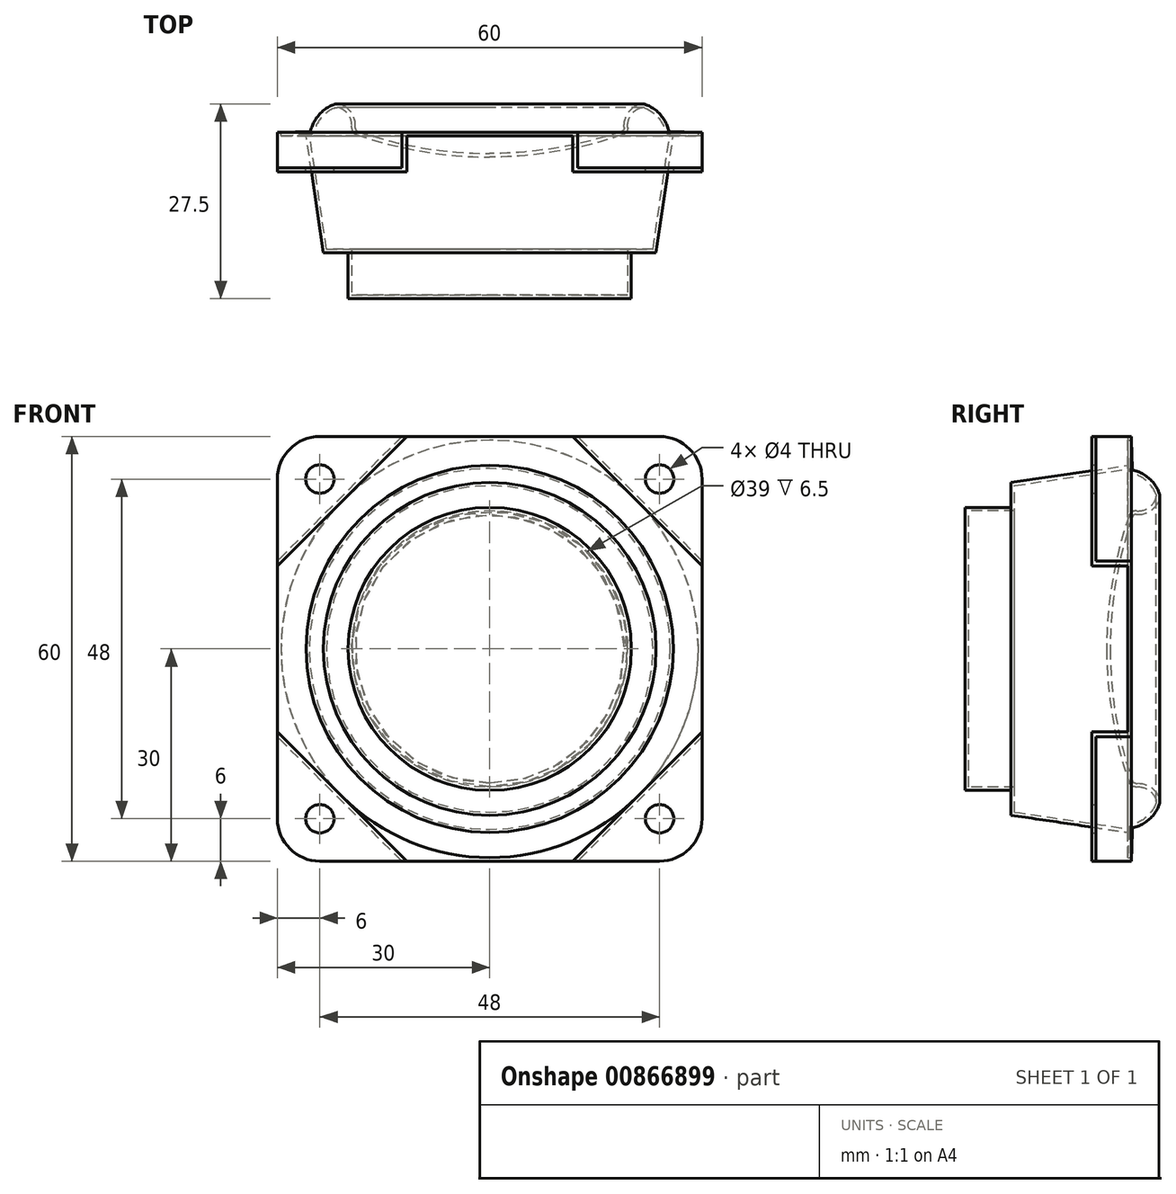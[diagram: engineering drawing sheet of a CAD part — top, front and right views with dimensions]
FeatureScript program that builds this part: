
annotation { "Feature Type Name" : "Feature", "Feature Type Description" : "" }
export const myFeature = defineFeature(function(context is Context, id is Id, definition is map)
    precondition{}
    {
        {
            var Q0;
            Q0=qCreatedBy(makeId("Front.planeOp"),FACE);
            var sketch = newSketch(context, id + "F0", { "sketchPlane" : qUnion([Q0])});
            skLineSegment(sketch, "E0.bottom", {"start": v(24, -30) * mm, "end": v(-24, -30) * mm});
            skLineSegment(sketch, "E0.top", {"start": v(24, 30) * mm, "end": v(-24, 30) * mm});
            skLineSegment(sketch, "E0.left", {"start": v(30, -24) * mm, "end": v(30, 24) * mm});
            skLineSegment(sketch, "E0.right", {"start": v(-30, -24) * mm, "end": v(-30, 24) * mm});
            skPoint(sketch, "E0.middle", {"position": v(0, 0) * mm});
            skPoint(sketch, "E1.visualSharp", {"position": v(-30, 30) * mm});
            skArc(sketch, "E1.filletArc", {"start": v(-24, 30) * mm, "mid": v(-28.24, 28.24) * mm, "end": v(-30, 24) * mm});
            skPoint(sketch, "E2.visualSharp", {"position": v(-30, -30) * mm});
            skArc(sketch, "E2.filletArc", {"start": v(-30, -24) * mm, "mid": v(-28.24, -28.24) * mm, "end": v(-24, -30) * mm});
            skPoint(sketch, "E3.visualSharp", {"position": v(30, -30) * mm});
            skArc(sketch, "E3.filletArc", {"start": v(24, -30) * mm, "mid": v(28.24, -28.24) * mm, "end": v(30, -24) * mm});
            skPoint(sketch, "E4.visualSharp", {"position": v(30, 30) * mm});
            skArc(sketch, "E4.filletArc", {"start": v(30, 24) * mm, "mid": v(28.24, 28.24) * mm, "end": v(24, 30) * mm});
            skLineSegment(sketch, "E5", {"start": v(-24, 24) * mm, "end": v(0, 0) * mm, "construction": true});
            skCircle(sketch, "E6", {"center": v(-24, 24) * mm, "radius": 2 * mm});
            skCircle(sketch, "E7", {"center": v(0, 0) * mm, "radius": 25.5 * mm});
            skCircle(sketch, "E8.1.0", {"center": v(-24, -24) * mm, "radius": 2 * mm});
            skCircle(sketch, "E8.2.0", {"center": v(24, -24) * mm, "radius": 2 * mm});
            skCircle(sketch, "E8.3.0", {"center": v(24, 24) * mm, "radius": 2 * mm});
            skSolve(sketch);
        }
        {
            var Q0;
            Q0 = qSketchRegion(id + "F0", true);
            extrude(context, id + "F1", {"entities" : qUnion([Q0]), "depth" : 5.6 * mm, "offsetDistance" : 25 * mm});
        }
        {
            var Q0;
            Q0=qCreatedBy(makeId("Front.planeOp"),FACE);
            var sketch = newSketch(context, id + "F2", { "sketchPlane" : qUnion([Q0])});
            skLineSegment(sketch, "E9.bottom", {"start": v(42.43, 0) * mm, "end": v(0, -42.43) * mm});
            skLineSegment(sketch, "E9.top", {"start": v(0, 42.43) * mm, "end": v(-42.43, 0) * mm});
            skLineSegment(sketch, "E9.left", {"start": v(42.43, 0) * mm, "end": v(0, 42.43) * mm});
            skLineSegment(sketch, "E9.right", {"start": v(0, -42.43) * mm, "end": v(-42.43, 0) * mm});
            skPoint(sketch, "E9.middle", {"position": v(0, 0) * mm});
            skLineSegment(sketch, "E10", {"start": v(-42.43, 0) * mm, "end": v(0, 0) * mm, "construction": true});
            skLineSegment(sketch, "E11.0", {"start": v(0, 41.72) * mm, "end": v(-41.72, 0) * mm});
            skLineSegment(sketch, "E11.1", {"start": v(41.72, 0) * mm, "end": v(0, 41.72) * mm});
            skLineSegment(sketch, "E11.2", {"start": v(41.72, 0) * mm, "end": v(0, -41.72) * mm});
            skLineSegment(sketch, "E11.3", {"start": v(0, -41.72) * mm, "end": v(-41.72, 0) * mm});
            skLineSegment(sketch, "E12.bottom", {"start": v(81.57, -52.25) * mm, "end": v(-81.57, -52.25) * mm});
            skLineSegment(sketch, "E12.top", {"start": v(81.57, 52.25) * mm, "end": v(-81.57, 52.25) * mm});
            skLineSegment(sketch, "E12.left", {"start": v(81.57, -52.25) * mm, "end": v(81.57, 52.25) * mm});
            skLineSegment(sketch, "E12.right", {"start": v(-81.57, -52.25) * mm, "end": v(-81.57, 52.25) * mm});
            skSolve(sketch);
        }
        {
            var Q0;
            Q0=makeQuery(id+"F2.imprint","IMPRINT",FACE,{"disambiguationData":[TD([[makeQuery(id+"F2.imprint","IMPRINT",EDGE,{"derivedFrom":sQuery(id+"F2.wireOp",EDGE,"E9.bottom")}),1.0]])]});
            extrude(context, id + "F3", {"entities" : qUnion([Q0]), "operationType" : NewBodyOperationType.REMOVE, "depth" : 5 * mm, "offsetDistance" : 25 * mm});
        }
        {
            var Q0;
            Q0=makeQuery(id+"F2.imprint","IMPRINT",FACE,{"disambiguationData":[TD([[makeQuery(id+"F2.imprint","IMPRINT",EDGE,{"derivedFrom":sQuery(id+"F2.wireOp",EDGE,"E11.0")}),1.0]])]});
            var Q1;
            Q1=makeQuery(id+"F1.opExtrude","CAP_FACE",FACE,{"disambiguationData":[OSD([sQuery(id+"F0.wireOp",EDGE,"E0.bottom"),sQuery(id+"F0.wireOp",EDGE,"E0.top"),sQuery(id+"F0.wireOp",EDGE,"E0.left"),sQuery(id+"F0.wireOp",EDGE,"E0.right"),sQuery(id+"F0.wireOp",EDGE,"E1.filletArc"),sQuery(id+"F0.wireOp",EDGE,"E2.filletArc"),sQuery(id+"F0.wireOp",EDGE,"E3.filletArc"),sQuery(id+"F0.wireOp",EDGE,"E4.filletArc"),sQuery(id+"F0.wireOp",EDGE,"E6"),sQuery(id+"F0.wireOp",EDGE,"E7"),sQuery(id+"F0.wireOp",EDGE,"E8.1.0"),sQuery(id+"F0.wireOp",EDGE,"E8.2.0"),sQuery(id+"F0.wireOp",EDGE,"E8.3.0")])],"isStart":false});
            extrude(context, id + "F4", {"entities" : qUnion([Q0]), "operationType" : NewBodyOperationType.REMOVE, "endBound" : BoundingType.UP_TO_SURFACE, "depth" : 25 * mm, "endBoundEntityFace" : qUnion([Q1]), "offsetDistance" : 25 * mm, "hasSecondDirection" : true, "secondDirectionOppositeDirection" : false, "secondDirectionDepth" : .5 * mm});
        }
        {
            var Q0;
            Q0=qCreatedBy(makeId("Right.planeOp"),FACE);
            var sketch = newSketch(context, id + "F5", { "sketchPlane" : qUnion([Q0])});
            skLineSegment(sketch, "E13", {"start": v(0, 26) * mm, "end": v(-17, 23.5) * mm});
            skLineSegment(sketch, "E14", {"start": v(-17, 23.5) * mm, "end": v(-17, 20) * mm});
            skLineSegment(sketch, "E15", {"start": v(-17, 20) * mm, "end": v(-23.5, 20) * mm});
            skLineSegment(sketch, "E16", {"start": v(-23.5, 20) * mm, "end": v(-23.5, 0) * mm});
            skLineSegment(sketch, "E17.0", {"start": v(-23, 19.5) * mm, "end": v(-23, 0) * mm});
            skLineSegment(sketch, "E17.1", {"start": v(-16.5, 19.5) * mm, "end": v(-23, 19.5) * mm});
            skLineSegment(sketch, "E17.2", {"start": v(-16.5, 23.07) * mm, "end": v(-16.5, 19.5) * mm});
            skLineSegment(sketch, "E17.3", {"start": v(0, 25.5) * mm, "end": v(-16.5, 23.07) * mm});
            skLineSegment(sketch, "E18", {"start": v(-23.5, 0) * mm, "end": v(-23, 0) * mm});
            skLineSegment(sketch, "E19", {"start": v(0, 26) * mm, "end": v(0, 25.5) * mm});
            skSolve(sketch);
        }
        {
            var Q0;
            Q0=makeQuery(id+"F5.imprint","IMPRINT",FACE,{"disambiguationData":[TD([[makeQuery(id+"F5.imprint","IMPRINT",EDGE,{"derivedFrom":sQuery(id+"F5.wireOp",EDGE,"E13")}),1.0]])]});
            var Q1;
            Q1=sQuery(id+"F5.wireOp",EDGE,"E18");
            revolve(context, id + "F6", {"operationType" : NewBodyOperationType.ADD, "surfaceOperationType" : NewSurfaceOperationType.NEW, "entities" : qUnion([Q0]), "axis" : qUnion([Q1]), "revolveType" : RevolveType.FULL});
        }
        {
            var Q0;
            Q0=qCreatedBy(makeId("Top.planeOp"),FACE);
            var sketch = newSketch(context, id + "F7", { "sketchPlane" : qUnion([Q0])});
            skLineSegment(sketch, "E20", {"start": v(29.5, 0) * mm, "end": v(25.5, 0.14) * mm});
            skArc(sketch, "E21", {"start": v(25.27, 0.33) * mm, "mid": v(24.1, 2.49) * mm, "end": v(22.1, 3.9) * mm});
            skArc(sketch, "E22", {"start": v(22.1, 3.9) * mm, "mid": v(21.54, 4) * mm, "end": v(20.99, 3.9) * mm});
            skArc(sketch, "E23", {"start": v(20.99, 3.9) * mm, "mid": v(19.46, 2.6) * mm, "end": v(19, 0.66) * mm});
            skArc(sketch, "E24", {"start": v(19, 0.66) * mm, "mid": v(18.92, 0.34) * mm, "end": v(18.67, 0.14) * mm});
            skLineSegment(sketch, "E25", {"start": v(0, -3) * mm, "end": v(-5.6, -3) * mm, "construction": true});
            skArc(sketch, "E26", {"start": v(0, -3) * mm, "mid": v(9.46, -2.2) * mm, "end": v(18.67, 0.14) * mm});
            skArc(sketch, "E27", {"start": v(25.5, 0.14) * mm, "mid": v(25.35, 0.2) * mm, "end": v(25.27, 0.33) * mm});
            skLineSegment(sketch, "E28", {"start": v(21.54, 4) * mm, "end": v(24.51, 4) * mm, "construction": true});
            skLineSegment(sketch, "E29.0", {"start": v(29.48, -0.5) * mm, "end": v(25.48, -0.36) * mm});
            skArc(sketch, "E29.1", {"start": v(25.48, -0.36) * mm, "mid": v(25.04, -0.2) * mm, "end": v(24.78, 0.2) * mm});
            skArc(sketch, "E29.2", {"start": v(24.78, 0.2) * mm, "mid": v(23.73, 2.15) * mm, "end": v(21.91, 3.43) * mm});
            skArc(sketch, "E29.3", {"start": v(0, -3.5) * mm, "mid": v(9.55, -2.7) * mm, "end": v(18.83, -0.33) * mm});
            skArc(sketch, "E29.4", {"start": v(19.5, 0.7) * mm, "mid": v(19.34, 0.07) * mm, "end": v(18.83, -0.33) * mm});
            skArc(sketch, "E29.5", {"start": v(21.17, 3.43) * mm, "mid": v(19.88, 2.34) * mm, "end": v(19.5, 0.7) * mm});
            skArc(sketch, "E29.6", {"start": v(21.91, 3.43) * mm, "mid": v(21.54, 3.5) * mm, "end": v(21.17, 3.43) * mm});
            skLineSegment(sketch, "E30", {"start": v(29.48, -0.5) * mm, "end": v(29.5, 0) * mm});
            skLineSegment(sketch, "E31", {"start": v(0, -3.5) * mm, "end": v(0, -3) * mm});
            skSolve(sketch);
        }
        {
            var Q0;
            Q0 = qSketchRegion(id + "F7", true);
            var Q1;
            Q1=sQuery(id+"F7.wireOp",EDGE,"E31");
            revolve(context, id + "F8", {"surfaceOperationType" : NewSurfaceOperationType.NEW, "entities" : qUnion([Q0]), "axis" : qUnion([Q1]), "revolveType" : RevolveType.FULL});
        }
    });
